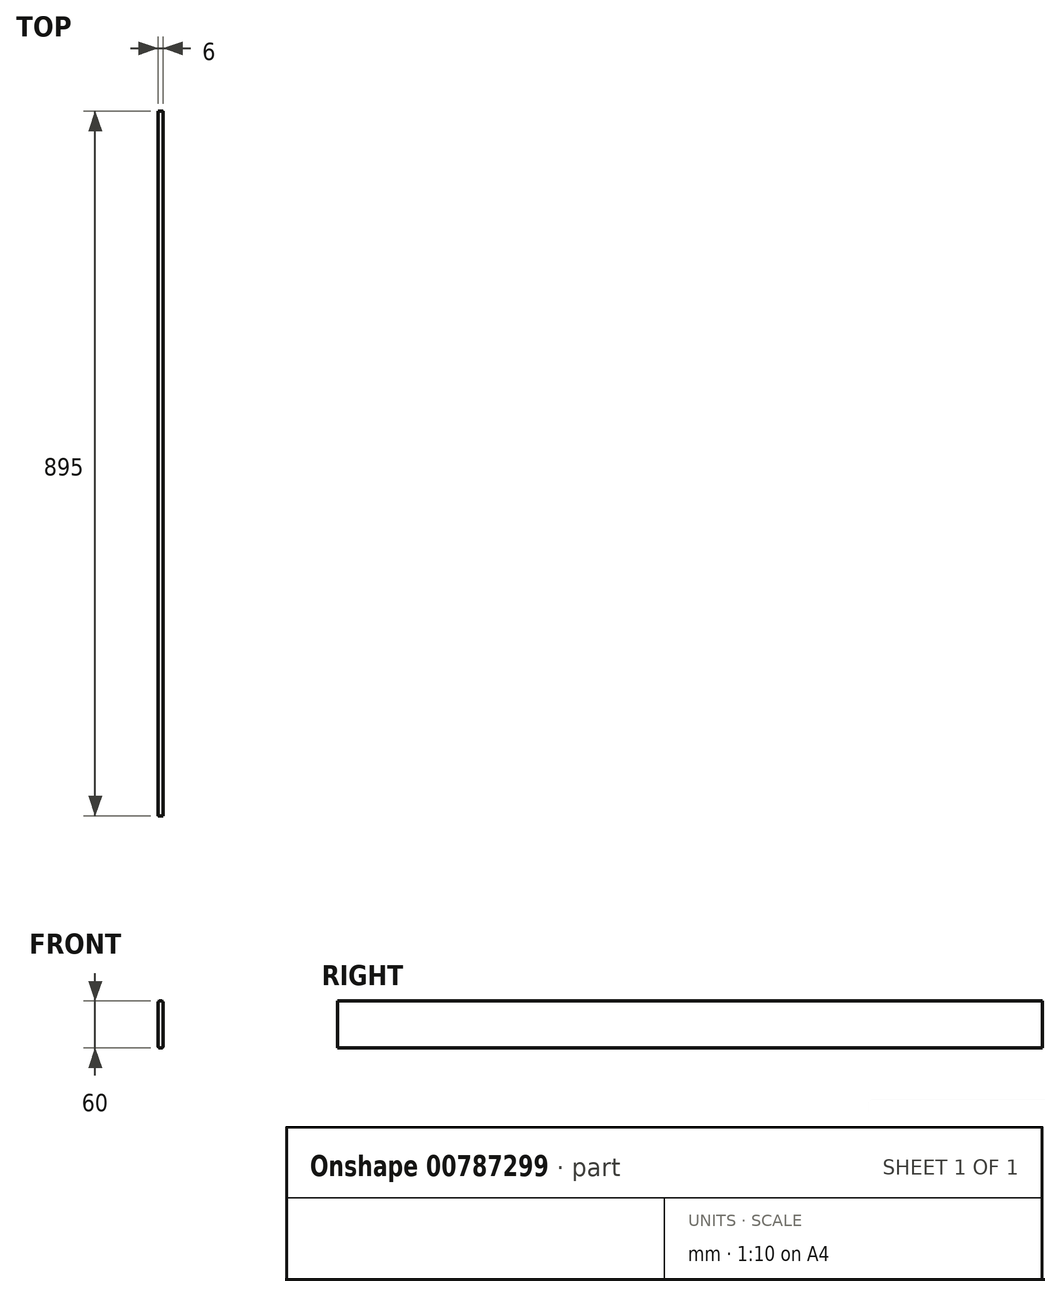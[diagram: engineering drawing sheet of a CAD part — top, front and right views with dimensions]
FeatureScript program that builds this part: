
annotation { "Feature Type Name" : "Feature", "Feature Type Description" : "" }
export const myFeature = defineFeature(function(context is Context, id is Id, definition is map)
    precondition{}
    {
        {
            var Q0;
            Q0=qCreatedBy(makeId("Front.planeOp"),FACE);
            var sketch = newSketch(context, id + "F0", { "sketchPlane" : qUnion([Q0])});
            skLineSegment(sketch, "E0.bottom", {"start": v(1, 30) * mm, "end": v(-1, 30) * mm});
            skLineSegment(sketch, "E0.top", {"start": v(1, -30) * mm, "end": v(-1, -30) * mm});
            skLineSegment(sketch, "E0.left", {"start": v(3, 28) * mm, "end": v(3, -28) * mm});
            skLineSegment(sketch, "E0.right", {"start": v(-3, 28) * mm, "end": v(-3, -28) * mm});
            skPoint(sketch, "E0.middle", {"position": v(0, 0) * mm});
            skPoint(sketch, "E1.visualSharp", {"position": v(-3, 30) * mm});
            skArc(sketch, "E1.filletArc", {"start": v(-1, 30) * mm, "mid": v(-2.41, 29.41) * mm, "end": v(-3, 28) * mm});
            skPoint(sketch, "E2.visualSharp", {"position": v(3, 30) * mm});
            skArc(sketch, "E2.filletArc", {"start": v(3, 28) * mm, "mid": v(2.41, 29.41) * mm, "end": v(1, 30) * mm});
            skPoint(sketch, "E3.visualSharp", {"position": v(3, -30) * mm});
            skArc(sketch, "E3.filletArc", {"start": v(1, -30) * mm, "mid": v(2.41, -29.41) * mm, "end": v(3, -28) * mm});
            skPoint(sketch, "E4.visualSharp", {"position": v(-3, -30) * mm});
            skArc(sketch, "E4.filletArc", {"start": v(-3, -28) * mm, "mid": v(-2.41, -29.41) * mm, "end": v(-1, -30) * mm});
            skLineSegment(sketch, "E5.0", {"start": v(0, 27) * mm, "end": v(0, -27) * mm});
            skLineSegment(sketch, "E5.1", {"start": v(0, 27) * mm, "end": v(0, 27) * mm});
            skLineSegment(sketch, "E5.2", {"start": v(0, 27) * mm, "end": v(0, -27) * mm});
            skLineSegment(sketch, "E5.3", {"start": v(0, -27) * mm, "end": v(0, -27) * mm});
            skSolve(sketch);
        }
        {
            var Q0;
            Q0=makeQuery(id+"F0.imprint","IMPRINT",FACE,{"disambiguationData":[TD([[makeQuery(id+"F0.imprint","IMPRINT",EDGE,{"derivedFrom":sQuery(id+"F0.wireOp",EDGE,"E0.bottom")}),1.0]])]});
            var Q1;
            Q1=makeQuery(id+"F0.imprint","IMPRINT",FACE,{"disambiguationData":[TD([[makeQuery(id+"F0.imprint","IMPRINT",EDGE,{"derivedFrom":sQuery(id+"F0.wireOp",EDGE,"E5.0")}),1.0]])]});
            extrude(context, id + "F1", {"entities" : qUnion([Q0, Q1]), "depth" : (900 - 5) * mm, "offsetDistance" : 25 * mm});
        }
    });
